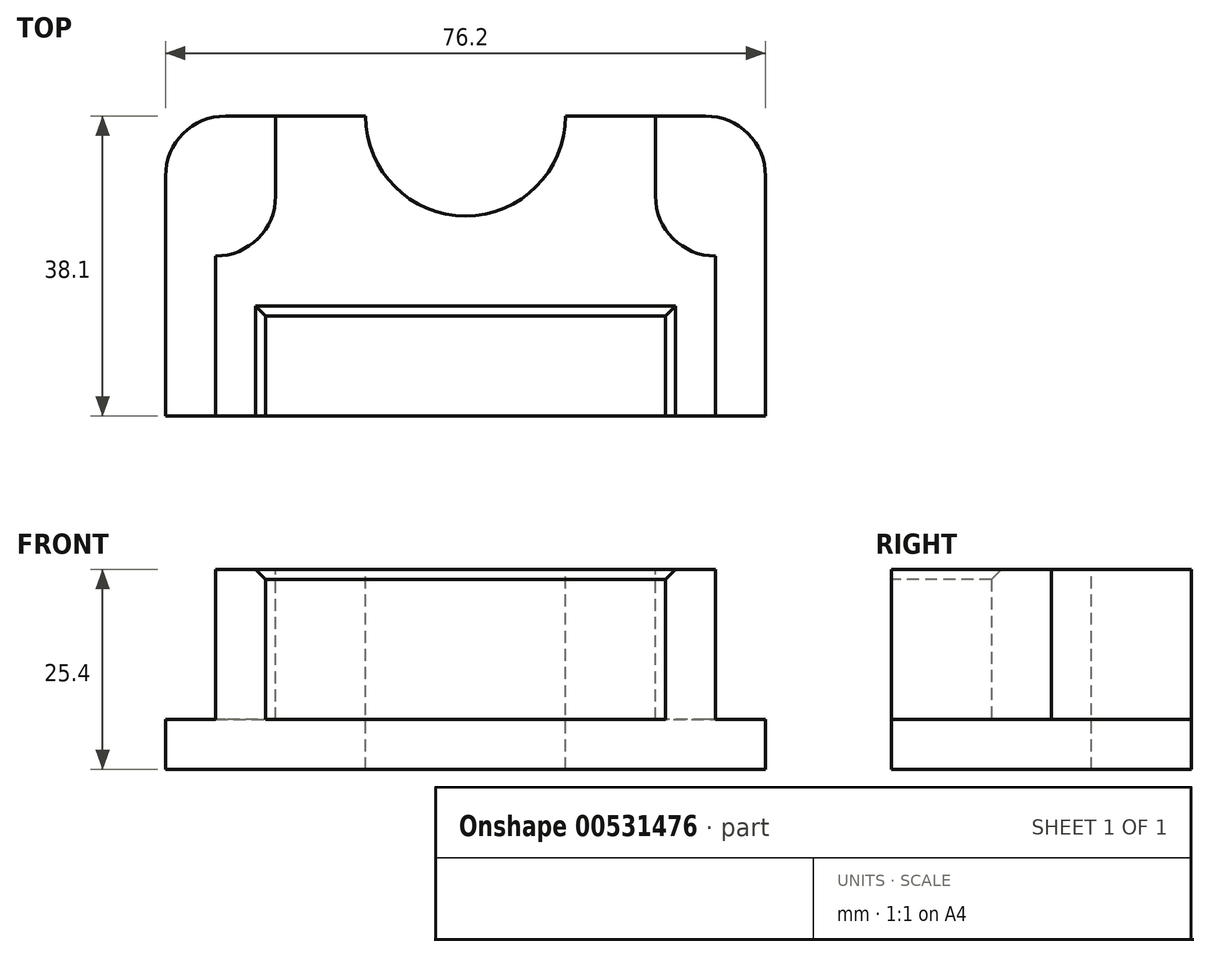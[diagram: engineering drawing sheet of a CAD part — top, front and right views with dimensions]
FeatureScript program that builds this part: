
annotation { "Feature Type Name" : "Feature", "Feature Type Description" : "" }
export const myFeature = defineFeature(function(context is Context, id is Id, definition is map)
    precondition{}
    {
        {
            var Q0;
            Q0=qCreatedBy(makeId("Top.planeOp"),FACE);
            var sketch = newSketch(context, id + "F0", { "sketchPlane" : qUnion([Q0])});
            skLineSegment(sketch, "E0.bottom", {"start": v(38.1, 19.05) * mm, "end": v(-38.1, 19.05) * mm});
            skLineSegment(sketch, "E0.top", {"start": v(38.1, -19.05) * mm, "end": v(-38.1, -19.05) * mm});
            skLineSegment(sketch, "E0.left", {"start": v(38.1, 19.05) * mm, "end": v(38.1, -19.05) * mm});
            skLineSegment(sketch, "E0.right", {"start": v(-38.1, 19.05) * mm, "end": v(-38.1, -19.05) * mm});
            skPoint(sketch, "E0.middle", {"position": v(0, 0) * mm});
            skSolve(sketch);
        }
        {
            var Q0;
            Q0=makeQuery(id+"F0.imprint","IMPRINT",FACE,{"disambiguationData":[TD([[makeQuery(id+"F0.imprint","IMPRINT",EDGE,{"derivedFrom":sQuery(id+"F0.wireOp",EDGE,"E0.bottom")}),1.0]])]});
            extrude(context, id + "F1", {"entities" : qUnion([Q0]), "depth" : 6.35 * mm, "offsetDistance" : 25.4 * mm});
        }
        {
            var Q0;
            Q0=makeQuery(id+"F1.opExtrude","CAP_FACE",FACE,{"disambiguationData":[OSD([sQuery(id+"F0.wireOp",EDGE,"E0.bottom"),sQuery(id+"F0.wireOp",EDGE,"E0.top"),sQuery(id+"F0.wireOp",EDGE,"E0.left"),sQuery(id+"F0.wireOp",EDGE,"E0.right")])],"isStart":false});
            var sketch = newSketch(context, id + "F2", { "sketchPlane" : qUnion([Q0])});
            skLineSegment(sketch, "E1.bottom", {"start": v(-31.75, 19.05) * mm, "end": v(31.75, 19.05) * mm});
            skLineSegment(sketch, "E1.top", {"start": v(-31.75, -19.05) * mm, "end": v(31.75, -19.05) * mm});
            skLineSegment(sketch, "E1.left", {"start": v(-31.75, 19.05) * mm, "end": v(-31.75, -19.05) * mm});
            skLineSegment(sketch, "E1.right", {"start": v(31.75, 19.05) * mm, "end": v(31.75, -19.05) * mm});
            skLineSegment(sketch, "E2.bottom", {"start": v(-25.4, -19.05) * mm, "end": v(25.4, -19.05) * mm});
            skLineSegment(sketch, "E2.top", {"start": v(-25.4, -6.35) * mm, "end": v(25.4, -6.35) * mm});
            skLineSegment(sketch, "E2.left", {"start": v(-25.4, -19.05) * mm, "end": v(-25.4, -6.35) * mm});
            skLineSegment(sketch, "E2.right", {"start": v(25.4, -19.05) * mm, "end": v(25.4, -6.35) * mm});
            skSolve(sketch);
        }
        {
            var Q0;
            Q0=makeQuery(id+"F2.imprint","IMPRINT",FACE,{"disambiguationData":[TD([[makeQuery(id+"F2.imprint","IMPRINT",EDGE,{"derivedFrom":sQuery(id+"F2.wireOp",EDGE,"E1.bottom")}),1.0]])]});
            extrude(context, id + "F3", {"entities" : qUnion([Q0]), "operationType" : NewBodyOperationType.ADD, "depth" : 19.05 * mm, "offsetDistance" : 25.4 * mm});
        }
        {
            var Q0;
            Q0=makeQuery(id+"F3.opExtrude","CAP_FACE",FACE,{"disambiguationData":[OSD([sQuery(id+"F2.wireOp",EDGE,"E1.bottom"),sQuery(id+"F2.wireOp",EDGE,"E1.top"),sQuery(id+"F2.wireOp",EDGE,"E1.left"),sQuery(id+"F2.wireOp",EDGE,"E1.right"),sQuery(id+"F2.wireOp",EDGE,"E2.top"),sQuery(id+"F2.wireOp",EDGE,"E2.left"),sQuery(id+"F2.wireOp",EDGE,"E2.right")])],"isStart":false});
            var sketch = newSketch(context, id + "F4", { "sketchPlane" : qUnion([Q0])});
            skCircle(sketch, "E3", {"center": v(0, 19.05) * mm, "radius": 12.7 * mm});
            skSolve(sketch);
        }
        {
            var Q0;
            {var subQ0=sQuery(id+"F4.wireOp",EDGE,"E3");var subQ1=makeQuery(id+"F3.opExtrude","CAP_EDGE",EDGE,{"disambiguationData":[OSD([sQuery(id+"F2.wireOp",EDGE,"E1.bottom")])],"isStart":false});var subQ2=makeQuery(id+"F4.imprint","INTERSECT",VERTEX,{"disambiguationData":[OD(0.0)],"derivedFrom":[subQ1,subQ0]});Q0=makeQuery(id+"F4.imprint","IMPRINT",FACE,{"disambiguationData":[TD([[makeQuery(id+"F4.imprint","IMPRINT",EDGE,{"disambiguationData":[TD([[subQ2,1.0]])],"derivedFrom":subQ0}),1.0]])]});}
            extrude(context, id + "F5", {"entities" : qUnion([Q0]), "operationType" : NewBodyOperationType.REMOVE, "endBound" : BoundingType.THROUGH_ALL, "oppositeDirection" : true, "depth" : 25.4 * mm, "offsetDistance" : 25.4 * mm});
        }
        {
            var Q0;
            Q0=makeQuery(id+"F3.opExtrude","CAP_FACE",FACE,{"disambiguationData":[OSD([sQuery(id+"F2.wireOp",EDGE,"E1.bottom"),sQuery(id+"F2.wireOp",EDGE,"E1.top"),sQuery(id+"F2.wireOp",EDGE,"E1.left"),sQuery(id+"F2.wireOp",EDGE,"E1.right"),sQuery(id+"F2.wireOp",EDGE,"E2.top"),sQuery(id+"F2.wireOp",EDGE,"E2.left"),sQuery(id+"F2.wireOp",EDGE,"E2.right")])],"isStart":false});
            var sketch = newSketch(context, id + "F6", { "sketchPlane" : qUnion([Q0])});
            skLineSegment(sketch, "E4.bottom", {"start": v(31.75, 19.05) * mm, "end": v(24.13, 19.05) * mm});
            skLineSegment(sketch, "E4.top", {"start": v(31.75, 8.9) * mm, "end": v(24.13, 8.9) * mm});
            skLineSegment(sketch, "E4.left", {"start": v(31.75, 19.05) * mm, "end": v(31.75, 8.9) * mm});
            skLineSegment(sketch, "E4.right", {"start": v(24.13, 19.05) * mm, "end": v(24.13, 8.9) * mm});
            skArc(sketch, "E5", {"start": v(24.13, 8.9) * mm, "mid": v(26.36, 3.5) * mm, "end": v(31.75, 1.27) * mm});
            skLineSegment(sketch, "E6.MirrorCS", {"start": v(-24.13, 19.05) * mm, "end": v(-24.13, 8.9) * mm});
            skArc(sketch, "E7.MirrorCS", {"start": v(-24.13, 8.9) * mm, "mid": v(-26.36, 3.5) * mm, "end": v(-31.75, 1.27) * mm});
            skSolve(sketch);
        }
        {
            var Q0;
            {var subQ0=sQuery(id+"F6.wireOp",EDGE,"E4.top");Q0=makeQuery(id+"F6.imprint","IMPRINT",FACE,{"disambiguationData":[TD([[makeQuery(id+"F6.imprint","IMPRINT",EDGE,{"derivedFrom":subQ0}),1.0]])]});}
            var Q1;
            Q1=makeQuery(id+"F6.imprint","IMPRINT",FACE,{"disambiguationData":[TD([[makeQuery(id+"F6.imprint","IMPRINT",EDGE,{"derivedFrom":sQuery(id+"F6.wireOp",EDGE,"E4.bottom")}),1.0]])]});
            var Q2;
            {var subQ0=sQuery(id+"F6.wireOp",EDGE,"E6.MirrorCS");Q2=makeQuery(id+"F6.imprint","IMPRINT",FACE,{"disambiguationData":[TD([[makeQuery(id+"F6.imprint","IMPRINT",EDGE,{"derivedFrom":subQ0}),-1.0]])]});}
            var Q3;
            {var subQ0=sQuery(id+"F0.wireOp",EDGE,"E0.top");var subQ1=sQuery(id+"F0.wireOp",EDGE,"E0.right");var subQ6=sQuery(id+"F0.wireOp",EDGE,"E0.bottom");Q3=makeQuery(id+"F3.boolean.opBoolean","SPLIT",FACE,{"disambiguationData":[TD([makeQuery(id+"F1.opExtrude","SWEPT_FACE",FACE,{"disambiguationData":[OSD([subQ1])]})])],"derivedFrom":makeQuery(id+"F1.opExtrude","CAP_FACE",FACE,{"disambiguationData":[OSD([subQ6,subQ0,sQuery(id+"F0.wireOp",EDGE,"E0.left"),subQ1])],"isStart":false})});}
            extrude(context, id + "F7", {"entities" : qUnion([Q0, Q1, Q2]), "operationType" : NewBodyOperationType.REMOVE, "endBound" : BoundingType.UP_TO_SURFACE, "oppositeDirection" : true, "depth" : 25.4 * mm, "endBoundEntityFace" : qUnion([Q3]), "offsetDistance" : 25.4 * mm});
        }
        {
            var Q0;
            Q0=makeQuery(id+"F3.opExtrude","CAP_EDGE",EDGE,{"disambiguationData":[OSD([sQuery(id+"F2.wireOp",EDGE,"E2.left")])],"isStart":false});
            var Q1;
            Q1=makeQuery(id+"F3.opExtrude","CAP_EDGE",EDGE,{"disambiguationData":[OSD([sQuery(id+"F2.wireOp",EDGE,"E2.top")])],"isStart":false});
            var Q2;
            Q2=makeQuery(id+"F3.opExtrude","CAP_EDGE",EDGE,{"disambiguationData":[OSD([sQuery(id+"F2.wireOp",EDGE,"E2.right")])],"isStart":false});
            chamfer(context, id + "F8", {"entities" : qUnion([Q0, Q1, Q2]), "width" : 1.27 * mm, "tangentPropagation" : true});
        }
        {
            var Q0;
            Q0=makeQuery(id+"F1.opExtrude","SWEPT_EDGE",EDGE,{"disambiguationData":[OSD([sQuery(id+"F0.wireOp",EDGE,"E0.bottom"),sQuery(id+"F0.wireOp",EDGE,"E0.right")])]});
            var Q1;
            Q1=makeQuery(id+"F1.opExtrude","SWEPT_EDGE",EDGE,{"disambiguationData":[OSD([sQuery(id+"F0.wireOp",EDGE,"E0.bottom"),sQuery(id+"F0.wireOp",EDGE,"E0.left")])]});
            fillet(context, id + "F9", {"entities" : qUnion([Q0, Q1]), "radius" : 7.62 * mm, "tangentPropagation" : true, "allowEdgeOverflow" : false});
        }
    });
